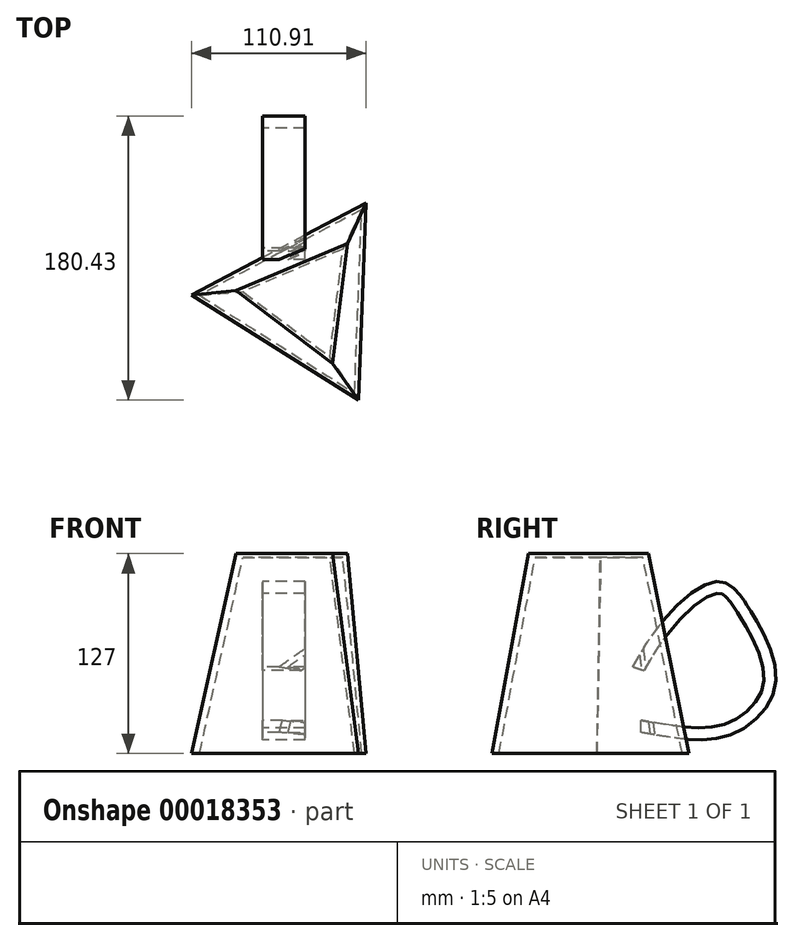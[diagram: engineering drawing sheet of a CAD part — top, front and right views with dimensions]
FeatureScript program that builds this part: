
annotation { "Feature Type Name" : "Feature", "Feature Type Description" : "" }
export const myFeature = defineFeature(function(context is Context, id is Id, definition is map)
    precondition{}
    {
        {
            var Q0;
            Q0=qCreatedBy(makeId("Top.planeOp"),FACE);
            var sketch = newSketch(context, id + "F0", { "sketchPlane" : qUnion([Q0])});
            skCircle(sketch, "E0.cCircle", {"center": v(0, 0) * mm, "radius": 36.18 * mm, "construction": true});
            skLineSegment(sketch, "E0.0", {"start": v(-72.31, 2.82) * mm, "end": v(38.6, 61.22) * mm});
            skLineSegment(sketch, "E0.1", {"start": v(38.6, 61.22) * mm, "end": v(33.71, -64.04) * mm});
            skLineSegment(sketch, "E0.2", {"start": v(33.71, -64.04) * mm, "end": v(-72.31, 2.82) * mm});
            skPoint(sketch, "E0.0.midPoint", {"position": v(-16.86, 32.02) * mm});
            skSolve(sketch);
        }
        {
            var Q0;
            Q0=qCreatedBy(makeId("Top.planeOp"),FACE);
            cPlane(context, id + "F1", {"entities" : qUnion([Q0]), "cplaneType" : CPlaneType.OFFSET, "offset" : 127 * mm, "width" : 152.4 * mm, "height" : 152.4 * mm});
        }
        {
            var Q0;
            Q0=qCreatedBy(id+"F1.planeOp",FACE);
            var sketch = newSketch(context, id + "F2", { "sketchPlane" : qUnion([Q0])});
            skCircle(sketch, "E1.cCircle", {"center": v(0, 0) * mm, "radius": 22.2 * mm, "construction": true});
            skLineSegment(sketch, "E1.0", {"start": v(-44.07, 5.42) * mm, "end": v(26.73, 35.45) * mm});
            skLineSegment(sketch, "E1.1", {"start": v(26.73, 35.45) * mm, "end": v(17.34, -40.87) * mm});
            skLineSegment(sketch, "E1.2", {"start": v(17.34, -40.87) * mm, "end": v(-44.07, 5.42) * mm});
            skPoint(sketch, "E1.0.midPoint", {"position": v(-8.67, 20.44) * mm});
            skSolve(sketch);
        }
        {
            var Q0;
            Q0=makeQuery(id+"F0.imprint","IMPRINT",FACE,{"disambiguationData":[TD([[makeQuery(id+"F0.imprint","IMPRINT",EDGE,{"derivedFrom":sQuery(id+"F0.wireOp",EDGE,"E0.0")}),-1.0]])]});
            var Q1;
            Q1=makeQuery(id+"F2.imprint","IMPRINT",FACE,{"disambiguationData":[TD([[makeQuery(id+"F2.imprint","IMPRINT",EDGE,{"derivedFrom":sQuery(id+"F2.wireOp",EDGE,"E1.0")}),-1.0]])]});
            loft(context, id + "F3", {"sheetProfilesArray" : [{ "sheetProfileEntities" : qUnion([Q0]) }, { "sheetProfileEntities" : qUnion([Q1]) }]});
        }
        {
            var Q0;
            Q0=makeQuery(id+"F3.opLoft","CAP_FACE",FACE,{"disambiguationData":[OSD([makeQuery(id+"F0.imprint","IMPRINT",FACE,{"disambiguationData":[TD([[makeQuery(id+"F0.imprint","IMPRINT",EDGE,{"derivedFrom":sQuery(id+"F0.wireOp",EDGE,"E0.0")}),-1.0]])]})])],"isStart":true});
            shell(context, id + "F4", {"entities" : qUnion([Q0]), "thickness" : 2.54 * mm});
        }
        {
            var Q0;
            Q0=qCreatedBy(makeId("Right.planeOp"),FACE);
            var sketch = newSketch(context, id + "F5", { "sketchPlane" : qUnion([Q0])});
            skFitSpline(sketch, "E2", {"points": [v(30.56, 11.95) * mm, v(87.7, 10.53) * mm, v(117.77, 46.75) * mm, v(100.96, 92.02) * mm, v(96.68, 98.64) * mm, v(81.72, 110.56) * mm, v(24, 55.53) * mm], "startDerivative": vector(320.87, -55.03) * mm, "endDerivative": vector(-227.88, -428.66) * mm});
            skSolve(sketch);
        }
        {
            var Q0;
            Q0=qCreatedBy(makeId("Front.planeOp"),FACE);
            cPlane(context, id + "F6", {"entities" : qUnion([Q0]), "cplaneType" : CPlaneType.OFFSET, "offset" : 40.64 * mm, "oppositeDirection" : true, "width" : 152.4 * mm, "height" : 152.4 * mm});
        }
        {
            var Q0;
            Q0=qCreatedBy(id+"F6.planeOp",FACE);
            var sketch = newSketch(context, id + "F7", { "sketchPlane" : qUnion([Q0])});
            skLineSegment(sketch, "E3.bottom", {"start": v(0, 11.64) * mm, "end": v(-27.28, 11.64) * mm});
            skLineSegment(sketch, "E3.top", {"start": v(0, 19.34) * mm, "end": v(-27.28, 19.34) * mm});
            skLineSegment(sketch, "E3.left", {"start": v(0, 11.64) * mm, "end": v(0, 19.34) * mm});
            skLineSegment(sketch, "E3.right", {"start": v(-27.28, 11.64) * mm, "end": v(-27.28, 19.34) * mm});
            skSolve(sketch);
        }
        {
            var Q0;
            Q0=makeQuery(id+"F7.imprint","IMPRINT",FACE,{"disambiguationData":[TD([[makeQuery(id+"F7.imprint","IMPRINT",EDGE,{"derivedFrom":sQuery(id+"F7.wireOp",EDGE,"E3.bottom")}),-1.0]])]});
            var Q1;
            Q1=sQuery(id+"F5.wireOp",EDGE,"E2");
            sweep(context, id + "F8", {"operationType" : NewBodyOperationType.ADD, "profiles" : qUnion([Q0]), "path" : qUnion([Q1])});
        }
    });
